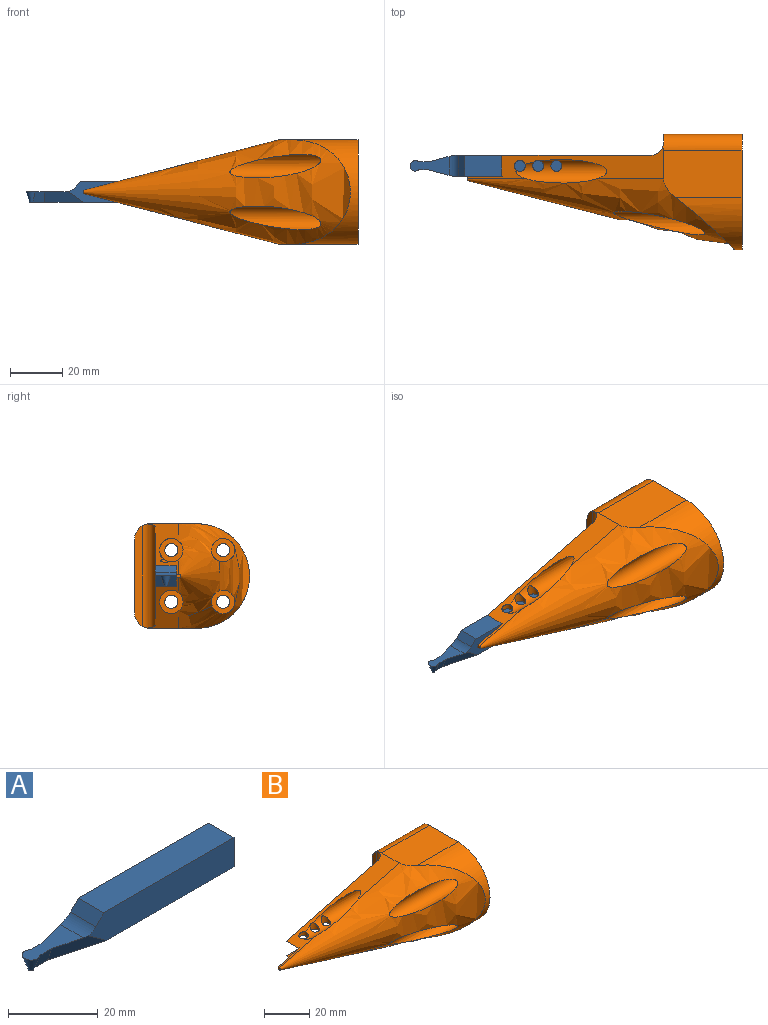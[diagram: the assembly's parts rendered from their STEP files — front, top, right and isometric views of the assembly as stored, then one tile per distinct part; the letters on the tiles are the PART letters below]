
ASSEMBLY  parts=2 mates=1
PART A: 13 faces, bbox 62.5x8.5x8.5 mm
  f0: plane 45.87x8mm, normal (0,1,0), area 343.9mm2, adj f1,f7,f8,f10,f11,f12
  f1: plane 14.98x4.17mm, normal (-0.24,0.91,-0.34), area 53.2mm2, adj f0,f2,f8,f9,f12
  f2: plane 5.12x4.47mm, normal (0,0.94,-0.34), area 17.5mm2, adj f1,f3,f8,f9
  f3: cone r=2mm half-angle=20deg, axis (0,0,1), area 28.2mm2, adj f2,f4,f8,f9
  f4: plane 5.12x4.47mm, normal (0,-0.94,-0.34), area 17.5mm2, adj f3,f5,f8,f9
  f5: plane 14.98x4.17mm, normal (-0.24,-0.91,-0.34), area 53.2mm2, adj f4,f6,f8,f9,f12
  f6: plane 45.87x8mm, normal (0,-1,0), area 343.9mm2, adj f5,f7,f8,f10,f11,f12
  f7: plane 8x8mm, normal (1,0,0), area 64mm2, adj f0,f6,f8,f10
  f8: plane 60.54x8mm, normal (0,0,-1), area 381.4mm2, adj f0,f1,f2,f3,f4,f5,f6,f7
  f9: plane 14.93x7.25mm, normal (0,0,1), area 62.8mm2, adj f1,f2,f3,f4,f5,f12
  f10: plane 41x8mm, normal (0,0,1), area 328mm2, adj f0,f6,f7,f11
  f11: plane 8x2.54mm, normal (-0.71,0,0.71), area 28.7mm2, adj f0,f6,f10,f12
  f12: cylinder r=5mm len=8mm, axis (0,1,0), area 31mm2, adj f0,f1,f5,f6,f9,f11
PART B: 33 faces, bbox 105x44x54 mm
  f0: cone r=20mm half-angle=14.5deg, axis (1,0,0), area 3059mm2, adj f1,f3,f4,f5,f6,f7,f22,f24
  f1: plane 75x19.4mm, normal (-0.25,0,-0.97), area 370.3mm2, adj f0,f2,f4,f7,f8,f13,f16,f17
  f2: plane 56.87x37.41mm, normal (0,1,0), area 1076.3mm2, adj f1,f3,f13,f14,f15,f17
  f3: plane 75.04x19.44mm, normal (-0.25,0,0.97), area 361mm2, adj f0,f2,f4,f5,f10,f15,f16,f17
  f4: plane 1.6x1.21mm, normal (-1,0,0), area 1.8mm2, adj f0,f1,f3,f16
  f5: plane 30x18mm, normal (0,0,1), area 529.1mm2, adj f0,f3,f6,f10,f11
  f6: cylinder r=20mm len=40mm, axis (-1,0,0), area 674.3mm2, adj f0,f5,f7,f11
  f7: plane 30x18mm, normal (0,0,-1), area 529.1mm2, adj f0,f1,f6,f8,f11
  f8: cylinder r=6mm len=30.38mm, axis (-1,0,0), area 283.1mm2, adj f1,f7,f9,f11,f12,f17
  f9: plane 30x28mm, normal (0,1,0), area 840mm2, adj f8,f10,f11,f12
  f10: cylinder r=6mm len=30.38mm, axis (-1,0,0), area 283.1mm2, adj f3,f5,f9,f11,f12,f17
  f11: plane 44x40mm, normal (1,0,0), area 1494.3mm2, adj f5,f6,f7,f8,f9,f10,f18,f19
  f12: plane 38.39x3mm, normal (-1,0,0), area 106.1mm2, adj f8,f9,f10,f17
  f13: plane 26.87x8mm, normal (0,0,1), area 214.9mm2, adj f1,f2,f14,f16
  f14: plane 8x8mm, normal (-1,0,0), area 64mm2, adj f2,f13,f15,f16
  f15: plane 26.87x8mm, normal (0,0,-1), area 173.4mm2, adj f2,f3,f14,f16,f30,f31,f32
  f16: plane 40x8mm, normal (0,1,0), area 275.4mm2, adj f1,f3,f4,f13,f14,f15
  f17: cylinder r=5mm len=39.8mm, axis (0,0,1), area 305.4mm2, adj f1,f2,f3,f8,f10,f12
  f18: cylinder r=2.5mm len=5mm, axis (1,0,0), area 62.8mm2, adj f11,f29
  f19: cylinder r=2.5mm len=5mm, axis (1,0,0), area 62.8mm2, adj f11,f27
  f20: cylinder r=2.5mm len=5mm, axis (1,0,0), area 62.8mm2, adj f11,f25
  f21: cylinder r=2.5mm len=5mm, axis (1,0,0), area 62.8mm2, adj f11,f23
  f22: cylinder r=4.5mm len=82.52mm, axis (-1,0,0), area 1837.3mm2, adj f0,f1,f23
  f23: plane 9x9mm, normal (-1,0,0), area 44mm2, adj f21,f22
  f24: cylinder r=4.5mm len=45.01mm, axis (-1,0,0), area 749.3mm2, adj f0,f25
  f25: plane 9x9mm, normal (-1,0,0), area 44mm2, adj f20,f24
  f26: cylinder r=4.5mm len=45.01mm, axis (-1,0,0), area 755mm2, adj f0,f27
  f27: plane 9x9mm, normal (-1,0,0), area 44mm2, adj f19,f26
  f28: cylinder r=4.5mm len=82.46mm, axis (-1,0,0), area 1798.6mm2, adj f0,f3,f29,f30,f31,f32
  f29: plane 9x9mm, normal (-1,0,0), area 44mm2, adj f18,f28
  f30: cylinder r=2.1mm len=4.29mm, axis (0,0,1), area 30.9mm2, adj f15,f28
  f31: cylinder r=2.1mm len=4.2mm, axis (0,0,1), area 29.8mm2, adj f3,f15,f28
  f32: cylinder r=2.1mm len=4.2mm, axis (0,0,1), area 21mm2, adj f3,f15,f28
PLACE A t=(-27.3,19.41,28.14)mm
PLACE B t=(67.7,15.41,28.14)mm
MATE fastened B.f14 <-> A.f7  axis (-1,0,0) through (32.7,19.41,28.14)mm
